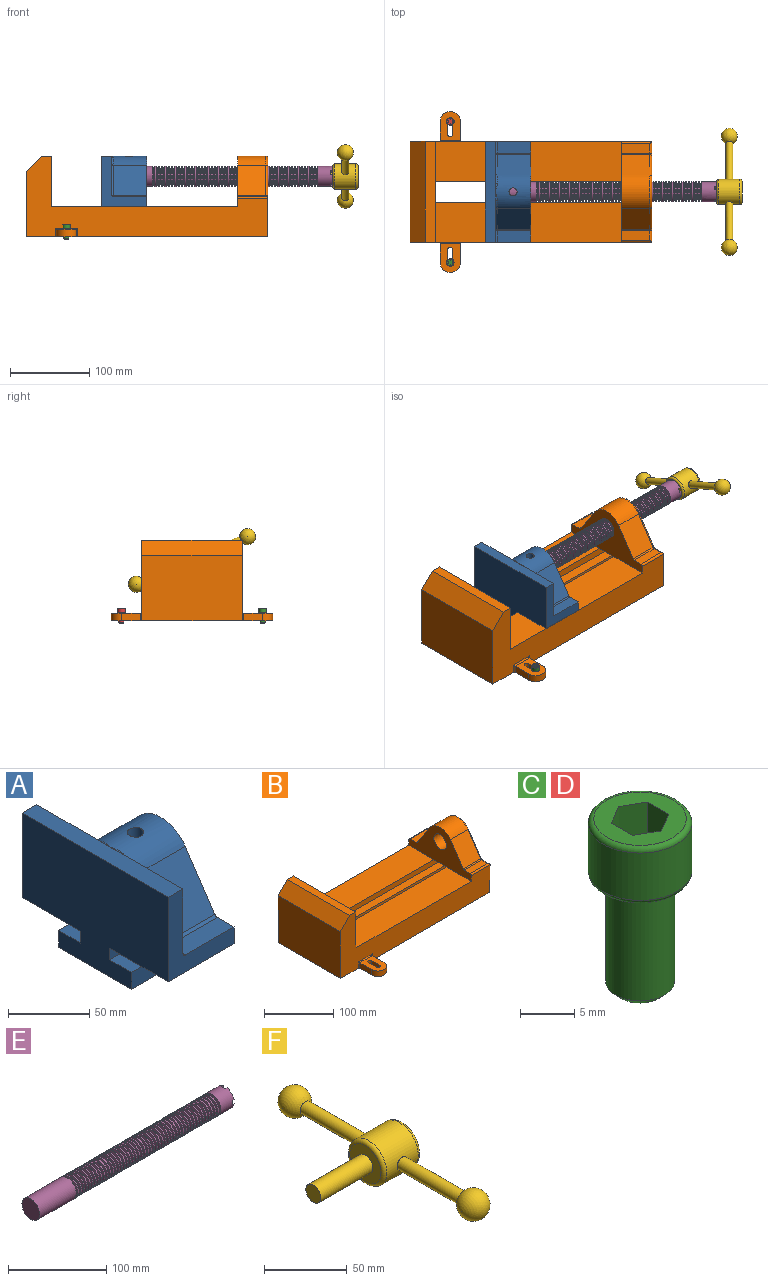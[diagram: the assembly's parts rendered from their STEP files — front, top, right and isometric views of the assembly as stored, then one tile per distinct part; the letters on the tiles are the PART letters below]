
ASSEMBLY  parts=6 mates=6
PART A: 36 faces, bbox 57.2x127x89 mm
  f0: plane 57.15x50.8mm, normal (0,0,-1), area 2903.2mm2, adj f6,f9,f10,f23
  f1: cylinder r=12.7mm len=44.45mm, axis (1,0,0), area 3464.3mm2, adj f6,f15,f16
  f2: plane 41.91x14.52mm, normal (0,0,1), area 608.5mm2, adj f6,f11,f24,f25
  f3: plane 51.86x48.26mm, normal (1,0,0), area 1495.7mm2, adj f8,f10,f31,f33,f35
  f4: plane 51.86x48.26mm, normal (1,0,0), area 1495.7mm2, adj f8,f11,f24,f28,f29
  f5: plane 57.15x50.8mm, normal (0,0,-1), area 2903.2mm2, adj f6,f9,f11,f22
  f6: plane 127x85.09mm, normal (1,0,0), area 5190.6mm2, adj f0,f1,f2,f5,f7,f10,f11,f12
  f7: plane 41.91x14.52mm, normal (0,0,1), area 608.5mm2, adj f6,f10,f30,f31
  f8: plane 127x12.7mm, normal (0,0,1), area 1612.9mm2, adj f3,f4,f9,f10,f11,f26,f34
  f9: plane 127x85.09mm, normal (-1,0,0), area 9096.8mm2, adj f0,f5,f8,f10,f11,f17,f18,f19
  f10: plane 63.5x57.15mm, normal (0,-1,0), area 1372.3mm2, adj f0,f3,f6,f7,f8,f9,f31
  f11: plane 63.5x57.15mm, normal (0,1,0), area 1372.3mm2, adj f2,f4,f5,f6,f8,f9,f24
  f12: plane 41.91x38.43mm, normal (0,-0.83,0.56), area 1939.2mm2, adj f6,f13,f30,f33
  f13: cylinder r=25.4mm len=44.45mm, axis (1,0,0), area 2026.5mm2, adj f6,f12,f14,f16,f26,f28,f34,f35
  f14: plane 41.91x38.43mm, normal (0,0.83,0.56), area 1939.2mm2, adj f6,f13,f25,f29
  f15: plane 25.4x25.4mm, normal (1,0,0), area 506.7mm2, adj f1
  f16: cylinder r=5.08mm len=13.76mm, axis (0,0,1), area 414mm2, adj f1,f13
  f17: plane 57.15x19.05mm, normal (0,0,1), area 1088.7mm2, adj f6,f9,f18,f23
  f18: plane 57.15x12.7mm, normal (0,-1,0), area 725.8mm2, adj f6,f9,f17,f19
  f19: plane 63.5x57.15mm, normal (0,0,-1), area 3629mm2, adj f6,f9,f18,f20
  f20: plane 57.15x12.7mm, normal (0,1,0), area 725.8mm2, adj f6,f9,f19,f21
  f21: plane 57.15x19.05mm, normal (0,0,1), area 1088.7mm2, adj f6,f9,f20,f22
  f22: plane 57.15x8.89mm, normal (0,1,0), area 508.1mm2, adj f5,f6,f9,f21
  f23: plane 57.15x8.89mm, normal (0,-1,0), area 508.1mm2, adj f0,f6,f9,f17
  f24: cylinder r=2.54mm len=14.52mm, axis (0,-1,0), area 57.9mm2, adj f2,f4,f11,f27
  f25: cylinder r=2.54mm len=41.91mm, axis (1,0,0), area 104.3mm2, adj f2,f6,f14,f27
  f26: bspline ~12.24x2.8mm, area 20.9mm2, adj f8,f13,f28
  f27: sphere r=2.54mm, area 6.3mm2, adj f24,f25,f29
  f28: torus R=27.94mm, axis (1,0,0), area 57.8mm2, adj f4,f13,f26,f29
  f29: cylinder r=2.54mm len=39.84mm, axis (0,-0.56,0.83), area 184.6mm2, adj f4,f14,f27,f28
  f30: cylinder r=2.54mm len=41.91mm, axis (1,0,0), area 104.3mm2, adj f6,f7,f12,f32
  f31: cylinder r=2.54mm len=14.52mm, axis (0,-1,0), area 57.9mm2, adj f3,f7,f10,f32
  f32: sphere r=2.54mm, area 6.3mm2, adj f30,f31,f33
  f33: cylinder r=2.54mm len=39.84mm, axis (0,-0.56,-0.83), area 184.6mm2, adj f3,f12,f32,f35
  f34: bspline ~12.24x2.8mm, area 20.9mm2, adj f8,f13,f35
  f35: torus R=27.94mm, axis (1,0,0), area 57.8mm2, adj f3,f13,f33,f34
PART B: 61 faces, bbox 304.8x203.2x103.7 mm
  f0: plane 304.8x101.6mm, normal (0,1,0), area 13520.3mm2, adj f3,f4,f5,f6,f7,f8,f9,f16
  f1: plane 304.8x101.6mm, normal (0,-1,0), area 13520.3mm2, adj f2,f3,f5,f6,f7,f8,f9,f16
  f2: plane 234.95x50.8mm, normal (0,0,1), area 11935.5mm2, adj f1,f5,f16,f26
  f3: plane 127x99.06mm, normal (1,0,0), area 7097.5mm2, adj f0,f1,f9,f14,f17,f18,f19,f20
  f4: plane 234.95x50.8mm, normal (0,0,1), area 11935.5mm2, adj f0,f5,f16,f27
  f5: plane 127x101.6mm, normal (1,0,0), area 9516.1mm2, adj f0,f1,f2,f4,f6,f9,f18,f19
  f6: plane 127x12.7mm, normal (0,0,1), area 1612.9mm2, adj f0,f1,f5,f7
  f7: plane 127x19.05mm, normal (-0.71,0,0.71), area 3421.5mm2, adj f0,f1,f6,f8
  f8: plane 127x82.55mm, normal (-1,0,0), area 10483.8mm2, adj f0,f1,f7,f9
  f9: plane 304.8x203.2mm, normal (0,0,-1), area 33298.3mm2, adj f0,f1,f3,f5,f8,f21,f22,f39
  f10: plane 35.56x11.98mm, normal (0,0,1), area 426mm2, adj f16,f28,f29,f30
  f11: plane 38.43x35.56mm, normal (0,0.83,0.56), area 1645.4mm2, adj f12,f16,f29,f32
  f12: cylinder r=25.4mm len=42.19mm, axis (1,0,0), area 1770.2mm2, adj f11,f13,f16,f33
  f13: plane 38.43x35.56mm, normal (0,-0.83,0.56), area 1645.4mm2, adj f12,f16,f34,f35
  f14: cylinder r=12.7mm len=38.1mm, axis (1,0,0), area 3040.2mm2, adj f3,f16
  f15: plane 35.56x11.98mm, normal (0,0,1), area 426mm2, adj f16,f34,f36,f38
  f16: plane 127x63.5mm, normal (-1,0,0), area 4155.5mm2, adj f0,f1,f2,f4,f10,f11,f12,f13
  f17: plane 38.1x25.4mm, normal (0,0,-1), area 967.7mm2, adj f3,f16,f26,f27
  f18: plane 273.05x19.05mm, normal (0,0,-1), area 5201.6mm2, adj f3,f5,f19,f26
  f19: plane 273.05x12.7mm, normal (0,1,0), area 3467.7mm2, adj f3,f5,f18,f20
  f20: plane 273.05x19.05mm, normal (0,0,1), area 5201.6mm2, adj f3,f5,f19,f21
  f21: plane 273.05x16.51mm, normal (0,1,0), area 4508.1mm2, adj f3,f5,f9,f20
  f22: plane 273.05x16.51mm, normal (0,-1,0), area 4508.1mm2, adj f3,f5,f9,f23
  f23: plane 273.05x19.05mm, normal (0,0,1), area 5201.6mm2, adj f3,f5,f22,f24
  f24: plane 273.05x12.7mm, normal (0,-1,0), area 3467.7mm2, adj f3,f5,f23,f25
  f25: plane 273.05x19.05mm, normal (0,0,-1), area 5201.6mm2, adj f3,f5,f24,f27
  f26: plane 273.05x8.89mm, normal (0,1,0), area 2427.4mm2, adj f2,f3,f5,f17,f18
  f27: plane 273.05x8.89mm, normal (0,-1,0), area 2427.4mm2, adj f3,f4,f5,f17,f25
  f28: cylinder r=2.54mm len=38.1mm, axis (1,0,0), area 148.3mm2, adj f0,f10,f16,f30
  f29: cylinder r=2.54mm len=35.56mm, axis (-1,0,0), area 88.5mm2, adj f10,f11,f16,f31
  f30: cylinder r=2.54mm len=14.52mm, axis (0,1,0), area 54.3mm2, adj f3,f10,f28,f31
  f31: torus R=5.08mm, axis (-1,0,0), area 13.5mm2, adj f3,f29,f30,f32
  f32: cylinder r=2.54mm len=39.84mm, axis (0,0.56,-0.83), area 184.6mm2, adj f3,f11,f31,f33
  f33: torus R=22.86mm, axis (-1,0,0), area 191.4mm2, adj f3,f12,f32,f35
  f34: cylinder r=2.54mm len=35.56mm, axis (-1,0,0), area 88.5mm2, adj f13,f15,f16,f37
  f35: cylinder r=2.54mm len=39.84mm, axis (0,0.56,0.83), area 184.6mm2, adj f3,f13,f33,f37
  f36: cylinder r=2.54mm len=38.1mm, axis (-1,0,0), area 148.3mm2, adj f1,f15,f16,f38
  f37: torus R=5.08mm, axis (-1,0,0), area 13.5mm2, adj f3,f34,f35,f38
  f38: cylinder r=2.54mm len=14.52mm, axis (0,1,0), area 54.3mm2, adj f3,f15,f36,f37
  f39: plane 23.88x9.53mm, normal (-1,0,0), area 227.4mm2, adj f9,f45,f46,f60
  f40: plane 23.88x9.53mm, normal (1,0,0), area 227.4mm2, adj f9,f45,f46,f58
  f41: cylinder r=3.3mm len=9.53mm, axis (0,0,-1), area 98.8mm2, adj f9,f42,f44,f46
  f42: plane 15.62x9.53mm, normal (-1,0,0), area 148.8mm2, adj f9,f41,f43,f46
  f43: cylinder r=3.3mm len=9.53mm, axis (0,0,-1), area 98.8mm2, adj f9,f42,f44,f46
  f44: plane 15.62x9.53mm, normal (1,0,0), area 148.8mm2, adj f9,f41,f43,f46
  f45: cylinder r=12.7mm len=25.4mm, axis (0,0,-1), area 380mm2, adj f9,f39,f40,f46
  f46: plane 36.58x25.4mm, normal (0,0,1), area 722.4mm2, adj f39,f40,f41,f42,f43,f44,f45,f59
  f47: plane 23.88x9.53mm, normal (-1,0,0), area 227.4mm2, adj f9,f53,f54,f56
  f48: plane 23.88x9.53mm, normal (1,0,0), area 227.4mm2, adj f9,f53,f54,f55
  f49: cylinder r=3.3mm len=9.53mm, axis (0,0,-1), area 98.8mm2, adj f9,f50,f52,f54
  f50: plane 15.62x9.53mm, normal (-1,0,0), area 148.8mm2, adj f9,f49,f51,f54
  f51: cylinder r=3.3mm len=9.53mm, axis (0,0,-1), area 98.8mm2, adj f9,f50,f52,f54
  f52: plane 15.62x9.53mm, normal (1,0,0), area 148.8mm2, adj f9,f49,f51,f54
  f53: cylinder r=12.7mm len=25.4mm, axis (0,0,-1), area 380mm2, adj f9,f47,f48,f54
  f54: plane 36.58x25.4mm, normal (0,0,1), area 722.4mm2, adj f47,f48,f49,f50,f51,f52,f53,f57
  f55: cylinder r=1.52mm len=11.05mm, axis (0,0,-1), area 24.1mm2, adj f0,f9,f48,f57
  f56: cylinder r=1.52mm len=11.05mm, axis (0,0,1), area 24.1mm2, adj f0,f9,f47,f57
  f57: cylinder r=1.52mm len=28.45mm, axis (1,0,0), area 63.5mm2, adj f0,f54,f55,f56
  f58: cylinder r=1.52mm len=11.05mm, axis (0,0,1), area 24.1mm2, adj f1,f9,f40,f59
  f59: cylinder r=1.52mm len=28.45mm, axis (-1,0,0), area 63.5mm2, adj f1,f46,f58,f60
  f60: cylinder r=1.52mm len=11.05mm, axis (0,0,-1), area 24.1mm2, adj f1,f9,f39,f59
PART C: 15 faces, bbox 10.3x10.3x19.1 mm
  f0: plane 8.51x8.51mm, normal (0,0,1), area 37.2mm2, adj f5,f6,f7,f8,f9,f10,f14
  f1: cylinder r=3.17mm len=11.94mm, axis (0,0,1), area 238.2mm2, adj f4,f12
  f2: plane 4.83x4.83mm, normal (0,0,-1), area 18.3mm2, adj f12
  f3: cylinder r=4.76mm len=9.53mm, axis (0,0,-1), area 159.6mm2, adj f13,f14
  f4: plane 8.51x8.51mm, normal (0,0,-1), area 25.2mm2, adj f1,f13
  f5: plane 4.83x2.38mm, normal (-0.5,-0.87,0), area 13.3mm2, adj f0,f6,f10,f11
  f6: plane 4.83x2.38mm, normal (0.5,-0.87,0), area 13.3mm2, adj f0,f5,f7,f11
  f7: plane 4.83x2.75mm, normal (1,0,0), area 13.3mm2, adj f0,f6,f8,f11
  f8: plane 4.83x2.38mm, normal (0.5,0.87,0), area 13.3mm2, adj f0,f7,f9,f11
  f9: plane 4.83x2.38mm, normal (-0.5,0.87,0), area 13.3mm2, adj f0,f8,f10,f11
  f10: plane 4.83x2.75mm, normal (-1,0,0), area 13.3mm2, adj f0,f5,f9,f11
  f11: plane 5.5x4.76mm, normal (0,0,1), area 19.6mm2, adj f5,f6,f7,f8,f9,f10
  f12: cone r=3.17mm half-angle=45deg, axis (0,0,1), area 18.9mm2, adj f1,f2
  f13: torus R=4.25mm, axis (0,0,1), area 23mm2, adj f3,f4
  f14: torus R=4.25mm, axis (0,0,1), area 23mm2, adj f0,f3
PART D: same geometry as C
PART E: 220 faces, bbox 279.4x25.4x25.4 mm
  f0: cylinder r=12.7mm len=25.4mm, axis (-1,0,0), area 1468.2mm2, adj f1,f2,f3,f5,f7,f208,f209,f210
  f1: plane 9.9x9.9mm, normal (1,0,0), area 62.3mm2, adj f0,f4,f213,f216
  f2: plane 9.9x9.9mm, normal (1,0,0), area 62.3mm2, adj f0,f4,f210,f218
  f3: plane 9.9x9.9mm, normal (1,0,0), area 62.3mm2, adj f0,f4,f209,f212
  f4: cylinder r=6.35mm len=25.4mm, axis (1,0,0), area 960.3mm2, adj f1,f2,f3,f5,f6,f208,f209,f210
  f5: plane 9.9x9.9mm, normal (1,0,0), area 62.3mm2, adj f0,f4,f215,f217
  f6: plane 12.7x12.7mm, normal (1,0,0), area 126.7mm2, adj f4
  f7: cone r=12.7mm half-angle=76deg, axis (1,0,0), area 188mm2, adj f0,f9
  f8: cone r=10.16mm half-angle=76deg, axis (-1,0,0), area 188mm2, adj f9,f10
  f9: cylinder r=10.16mm len=20.32mm, axis (1,0,0), area 81.1mm2, adj f7,f8
  f10: cylinder r=12.7mm len=25.4mm, axis (-1,0,0), area 131.7mm2, adj f8,f11
  f11: cone r=12.7mm half-angle=76deg, axis (1,0,0), area 188mm2, adj f10,f13
  f12: cone r=10.16mm half-angle=76deg, axis (-1,0,0), area 188mm2, adj f13,f14
  f13: cylinder r=10.16mm len=20.32mm, axis (1,0,0), area 81.1mm2, adj f11,f12
  f14: cylinder r=12.7mm len=25.4mm, axis (-1,0,0), area 131.7mm2, adj f12,f15
  f15: cone r=12.7mm half-angle=76deg, axis (1,0,0), area 188mm2, adj f14,f17
  f16: cone r=10.16mm half-angle=76deg, axis (-1,0,0), area 188mm2, adj f17,f18
  f17: cylinder r=10.16mm len=20.32mm, axis (1,0,0), area 81.1mm2, adj f15,f16
  f18: cylinder r=12.7mm len=25.4mm, axis (-1,0,0), area 131.7mm2, adj f16,f19
  f19: cone r=12.7mm half-angle=76deg, axis (1,0,0), area 188mm2, adj f18,f21
  f20: cone r=10.16mm half-angle=76deg, axis (-1,0,0), area 188mm2, adj f21,f22
  f21: cylinder r=10.16mm len=20.32mm, axis (1,0,0), area 81.1mm2, adj f19,f20
  f22: cylinder r=12.7mm len=25.4mm, axis (-1,0,0), area 131.7mm2, adj f20,f23
  f23: cone r=12.7mm half-angle=76deg, axis (1,0,0), area 188mm2, adj f22,f25
  f24: cone r=10.16mm half-angle=76deg, axis (-1,0,0), area 188mm2, adj f25,f26
  f25: cylinder r=10.16mm len=20.32mm, axis (1,0,0), area 81.1mm2, adj f23,f24
  f26: cylinder r=12.7mm len=25.4mm, axis (-1,0,0), area 131.7mm2, adj f24,f27
  f27: cone r=12.7mm half-angle=76deg, axis (1,0,0), area 188mm2, adj f26,f29
  f28: cone r=10.16mm half-angle=76deg, axis (-1,0,0), area 188mm2, adj f29,f30
  f29: cylinder r=10.16mm len=20.32mm, axis (1,0,0), area 81.1mm2, adj f27,f28
  f30: cylinder r=12.7mm len=25.4mm, axis (-1,0,0), area 131.7mm2, adj f28,f31
  f31: cone r=12.7mm half-angle=76deg, axis (1,0,0), area 188mm2, adj f30,f33
  f32: cone r=10.16mm half-angle=76deg, axis (-1,0,0), area 188mm2, adj f33,f34
  f33: cylinder r=10.16mm len=20.32mm, axis (1,0,0), area 81.1mm2, adj f31,f32
  f34: cylinder r=12.7mm len=25.4mm, axis (-1,0,0), area 131.7mm2, adj f32,f35
  f35: cone r=12.7mm half-angle=76deg, axis (1,0,0), area 188mm2, adj f34,f37
  f36: cone r=10.16mm half-angle=76deg, axis (-1,0,0), area 188mm2, adj f37,f38
  f37: cylinder r=10.16mm len=20.32mm, axis (1,0,0), area 81.1mm2, adj f35,f36
  f38: cylinder r=12.7mm len=25.4mm, axis (-1,0,0), area 131.7mm2, adj f36,f39
  f39: cone r=12.7mm half-angle=76deg, axis (1,0,0), area 188mm2, adj f38,f41
  f40: cone r=10.16mm half-angle=76deg, axis (-1,0,0), area 188mm2, adj f41,f42
  f41: cylinder r=10.16mm len=20.32mm, axis (1,0,0), area 81.1mm2, adj f39,f40
  f42: cylinder r=12.7mm len=25.4mm, axis (-1,0,0), area 131.7mm2, adj f40,f43
  f43: cone r=12.7mm half-angle=76deg, axis (1,0,0), area 188mm2, adj f42,f45
  f44: cone r=10.16mm half-angle=76deg, axis (-1,0,0), area 188mm2, adj f45,f46
  f45: cylinder r=10.16mm len=20.32mm, axis (1,0,0), area 81.1mm2, adj f43,f44
  f46: cylinder r=12.7mm len=25.4mm, axis (-1,0,0), area 131.7mm2, adj f44,f47
  f47: cone r=12.7mm half-angle=76deg, axis (1,0,0), area 188mm2, adj f46,f49
  f48: cone r=10.16mm half-angle=76deg, axis (-1,0,0), area 188mm2, adj f49,f50
  f49: cylinder r=10.16mm len=20.32mm, axis (1,0,0), area 81.1mm2, adj f47,f48
  f50: cylinder r=12.7mm len=25.4mm, axis (-1,0,0), area 131.7mm2, adj f48,f51
  f51: cone r=12.7mm half-angle=76deg, axis (1,0,0), area 188mm2, adj f50,f53
  f52: cone r=10.16mm half-angle=76deg, axis (-1,0,0), area 188mm2, adj f53,f54
  f53: cylinder r=10.16mm len=20.32mm, axis (1,0,0), area 81.1mm2, adj f51,f52
  f54: cylinder r=12.7mm len=25.4mm, axis (-1,0,0), area 131.7mm2, adj f52,f55
  f55: cone r=12.7mm half-angle=76deg, axis (1,0,0), area 188mm2, adj f54,f57
  f56: cone r=10.16mm half-angle=76deg, axis (-1,0,0), area 188mm2, adj f57,f58
  f57: cylinder r=10.16mm len=20.32mm, axis (1,0,0), area 81.1mm2, adj f55,f56
  f58: cylinder r=12.7mm len=25.4mm, axis (-1,0,0), area 131.7mm2, adj f56,f59
  f59: cone r=12.7mm half-angle=76deg, axis (1,0,0), area 188mm2, adj f58,f61
  f60: cone r=10.16mm half-angle=76deg, axis (-1,0,0), area 188mm2, adj f61,f62
  f61: cylinder r=10.16mm len=20.32mm, axis (1,0,0), area 81.1mm2, adj f59,f60
  f62: cylinder r=12.7mm len=25.4mm, axis (-1,0,0), area 131.7mm2, adj f60,f63
  f63: cone r=12.7mm half-angle=76deg, axis (1,0,0), area 188mm2, adj f62,f65
  f64: cone r=10.16mm half-angle=76deg, axis (-1,0,0), area 188mm2, adj f65,f66
  f65: cylinder r=10.16mm len=20.32mm, axis (1,0,0), area 81.1mm2, adj f63,f64
  f66: cylinder r=12.7mm len=25.4mm, axis (-1,0,0), area 131.7mm2, adj f64,f67
  f67: cone r=12.7mm half-angle=76deg, axis (1,0,0), area 188mm2, adj f66,f69
  f68: cone r=10.16mm half-angle=76deg, axis (-1,0,0), area 188mm2, adj f69,f70
  f69: cylinder r=10.16mm len=20.32mm, axis (1,0,0), area 81.1mm2, adj f67,f68
  f70: cylinder r=12.7mm len=25.4mm, axis (-1,0,0), area 131.7mm2, adj f68,f71
  f71: cone r=12.7mm half-angle=76deg, axis (1,0,0), area 188mm2, adj f70,f73
  f72: cone r=10.16mm half-angle=76deg, axis (-1,0,0), area 188mm2, adj f73,f74
  f73: cylinder r=10.16mm len=20.32mm, axis (1,0,0), area 81.1mm2, adj f71,f72
  f74: cylinder r=12.7mm len=25.4mm, axis (-1,0,0), area 131.7mm2, adj f72,f75
  f75: cone r=12.7mm half-angle=76deg, axis (1,0,0), area 188mm2, adj f74,f77
  f76: cone r=10.16mm half-angle=76deg, axis (-1,0,0), area 188mm2, adj f77,f78
  f77: cylinder r=10.16mm len=20.32mm, axis (1,0,0), area 81.1mm2, adj f75,f76
  f78: cylinder r=12.7mm len=25.4mm, axis (-1,0,0), area 131.7mm2, adj f76,f79
  f79: cone r=12.7mm half-angle=76deg, axis (1,0,0), area 188mm2, adj f78,f81
  f80: cone r=10.16mm half-angle=76deg, axis (-1,0,0), area 188mm2, adj f81,f82
  f81: cylinder r=10.16mm len=20.32mm, axis (1,0,0), area 81.1mm2, adj f79,f80
  f82: cylinder r=12.7mm len=25.4mm, axis (-1,0,0), area 131.7mm2, adj f80,f83
  f83: cone r=12.7mm half-angle=76deg, axis (1,0,0), area 188mm2, adj f82,f85
  f84: cone r=10.16mm half-angle=76deg, axis (-1,0,0), area 188mm2, adj f85,f86
  f85: cylinder r=10.16mm len=20.32mm, axis (1,0,0), area 81.1mm2, adj f83,f84
  f86: cylinder r=12.7mm len=25.4mm, axis (-1,0,0), area 131.7mm2, adj f84,f87
  f87: cone r=12.7mm half-angle=76deg, axis (1,0,0), area 188mm2, adj f86,f89
  f88: cone r=10.16mm half-angle=76deg, axis (-1,0,0), area 188mm2, adj f89,f90
  f89: cylinder r=10.16mm len=20.32mm, axis (1,0,0), area 81.1mm2, adj f87,f88
  f90: cylinder r=12.7mm len=25.4mm, axis (-1,0,0), area 131.7mm2, adj f88,f91
  f91: cone r=12.7mm half-angle=76deg, axis (1,0,0), area 188mm2, adj f90,f93
  f92: cone r=10.16mm half-angle=76deg, axis (-1,0,0), area 188mm2, adj f93,f94
  f93: cylinder r=10.16mm len=20.32mm, axis (1,0,0), area 81.1mm2, adj f91,f92
  f94: cylinder r=12.7mm len=25.4mm, axis (-1,0,0), area 131.7mm2, adj f92,f95
  f95: cone r=12.7mm half-angle=76deg, axis (1,0,0), area 188mm2, adj f94,f97
  f96: cone r=10.16mm half-angle=76deg, axis (-1,0,0), area 188mm2, adj f97,f98
  f97: cylinder r=10.16mm len=20.32mm, axis (1,0,0), area 81.1mm2, adj f95,f96
  f98: cylinder r=12.7mm len=25.4mm, axis (-1,0,0), area 131.7mm2, adj f96,f99
  f99: cone r=12.7mm half-angle=76deg, axis (1,0,0), area 188mm2, adj f98,f101
  f100: cone r=10.16mm half-angle=76deg, axis (-1,0,0), area 188mm2, adj f101,f102
  f101: cylinder r=10.16mm len=20.32mm, axis (1,0,0), area 81.1mm2, adj f99,f100
  f102: cylinder r=12.7mm len=25.4mm, axis (-1,0,0), area 131.7mm2, adj f100,f103
  f103: cone r=12.7mm half-angle=76deg, axis (1,0,0), area 188mm2, adj f102,f105
  f104: cone r=10.16mm half-angle=76deg, axis (-1,0,0), area 188mm2, adj f105,f106
  f105: cylinder r=10.16mm len=20.32mm, axis (1,0,0), area 81.1mm2, adj f103,f104
  f106: cylinder r=12.7mm len=25.4mm, axis (-1,0,0), area 131.7mm2, adj f104,f107
  f107: cone r=12.7mm half-angle=76deg, axis (1,0,0), area 188mm2, adj f106,f109
  f108: cone r=10.16mm half-angle=76deg, axis (-1,0,0), area 188mm2, adj f109,f110
  f109: cylinder r=10.16mm len=20.32mm, axis (1,0,0), area 81.1mm2, adj f107,f108
  f110: cylinder r=12.7mm len=25.4mm, axis (-1,0,0), area 131.7mm2, adj f108,f111
  f111: cone r=12.7mm half-angle=76deg, axis (1,0,0), area 188mm2, adj f110,f113
  f112: cone r=10.16mm half-angle=76deg, axis (-1,0,0), area 188mm2, adj f113,f114
  f113: cylinder r=10.16mm len=20.32mm, axis (1,0,0), area 81.1mm2, adj f111,f112
  f114: cylinder r=12.7mm len=25.4mm, axis (-1,0,0), area 131.7mm2, adj f112,f115
  f115: cone r=12.7mm half-angle=76deg, axis (1,0,0), area 188mm2, adj f114,f117
  f116: cone r=10.16mm half-angle=76deg, axis (-1,0,0), area 188mm2, adj f117,f118
  f117: cylinder r=10.16mm len=20.32mm, axis (1,0,0), area 81.1mm2, adj f115,f116
  f118: cylinder r=12.7mm len=25.4mm, axis (-1,0,0), area 131.7mm2, adj f116,f119
  f119: cone r=12.7mm half-angle=76deg, axis (1,0,0), area 188mm2, adj f118,f121
  f120: cone r=10.16mm half-angle=76deg, axis (-1,0,0), area 188mm2, adj f121,f122
  f121: cylinder r=10.16mm len=20.32mm, axis (1,0,0), area 81.1mm2, adj f119,f120
  f122: cylinder r=12.7mm len=25.4mm, axis (-1,0,0), area 131.7mm2, adj f120,f123
  f123: cone r=12.7mm half-angle=76deg, axis (1,0,0), area 188mm2, adj f122,f125
  f124: cone r=10.16mm half-angle=76deg, axis (-1,0,0), area 188mm2, adj f125,f126
  f125: cylinder r=10.16mm len=20.32mm, axis (1,0,0), area 81.1mm2, adj f123,f124
  f126: cylinder r=12.7mm len=25.4mm, axis (-1,0,0), area 131.7mm2, adj f124,f127
  f127: cone r=12.7mm half-angle=76deg, axis (1,0,0), area 188mm2, adj f126,f129
  f128: cone r=10.16mm half-angle=76deg, axis (-1,0,0), area 188mm2, adj f129,f130
  f129: cylinder r=10.16mm len=20.32mm, axis (1,0,0), area 81.1mm2, adj f127,f128
  f130: cylinder r=12.7mm len=25.4mm, axis (-1,0,0), area 131.7mm2, adj f128,f131
  f131: cone r=12.7mm half-angle=76deg, axis (1,0,0), area 188mm2, adj f130,f133
  f132: cone r=10.16mm half-angle=76deg, axis (-1,0,0), area 188mm2, adj f133,f134
  f133: cylinder r=10.16mm len=20.32mm, axis (1,0,0), area 81.1mm2, adj f131,f132
  f134: cylinder r=12.7mm len=25.4mm, axis (-1,0,0), area 131.7mm2, adj f132,f135
  f135: cone r=12.7mm half-angle=76deg, axis (1,0,0), area 188mm2, adj f134,f137
  f136: cone r=10.16mm half-angle=76deg, axis (-1,0,0), area 188mm2, adj f137,f138
  f137: cylinder r=10.16mm len=20.32mm, axis (1,0,0), area 81.1mm2, adj f135,f136
  f138: cylinder r=12.7mm len=25.4mm, axis (-1,0,0), area 131.7mm2, adj f136,f139
  f139: cone r=12.7mm half-angle=76deg, axis (1,0,0), area 188mm2, adj f138,f141
  f140: cone r=10.16mm half-angle=76deg, axis (-1,0,0), area 188mm2, adj f141,f142
  f141: cylinder r=10.16mm len=20.32mm, axis (1,0,0), area 81.1mm2, adj f139,f140
  f142: cylinder r=12.7mm len=25.4mm, axis (-1,0,0), area 131.7mm2, adj f140,f143
  f143: cone r=12.7mm half-angle=76deg, axis (1,0,0), area 188mm2, adj f142,f145
  f144: cone r=10.16mm half-angle=76deg, axis (-1,0,0), area 188mm2, adj f145,f146
  f145: cylinder r=10.16mm len=20.32mm, axis (1,0,0), area 81.1mm2, adj f143,f144
  f146: cylinder r=12.7mm len=25.4mm, axis (-1,0,0), area 131.7mm2, adj f144,f147
  f147: cone r=12.7mm half-angle=76deg, axis (1,0,0), area 188mm2, adj f146,f149
  f148: cone r=10.16mm half-angle=76deg, axis (-1,0,0), area 188mm2, adj f149,f150
  f149: cylinder r=10.16mm len=20.32mm, axis (1,0,0), area 81.1mm2, adj f147,f148
  f150: cylinder r=12.7mm len=25.4mm, axis (-1,0,0), area 131.7mm2, adj f148,f151
  f151: cone r=12.7mm half-angle=76deg, axis (1,0,0), area 188mm2, adj f150,f153
  f152: cone r=10.16mm half-angle=76deg, axis (-1,0,0), area 188mm2, adj f153,f154
  f153: cylinder r=10.16mm len=20.32mm, axis (1,0,0), area 81.1mm2, adj f151,f152
  f154: cylinder r=12.7mm len=25.4mm, axis (-1,0,0), area 131.7mm2, adj f152,f155
  f155: cone r=12.7mm half-angle=76deg, axis (1,0,0), area 188mm2, adj f154,f157
  f156: cone r=10.16mm half-angle=76deg, axis (-1,0,0), area 188mm2, adj f157,f158
  f157: cylinder r=10.16mm len=20.32mm, axis (1,0,0), area 81.1mm2, adj f155,f156
  f158: cylinder r=12.7mm len=25.4mm, axis (-1,0,0), area 131.7mm2, adj f156,f159
  f159: cone r=12.7mm half-angle=76deg, axis (1,0,0), area 188mm2, adj f158,f161
  f160: cone r=10.16mm half-angle=76deg, axis (-1,0,0), area 188mm2, adj f161,f162
  f161: cylinder r=10.16mm len=20.32mm, axis (1,0,0), area 81.1mm2, adj f159,f160
  f162: cylinder r=12.7mm len=25.4mm, axis (-1,0,0), area 131.7mm2, adj f160,f163
  f163: cone r=12.7mm half-angle=76deg, axis (1,0,0), area 188mm2, adj f162,f165
  f164: cone r=10.16mm half-angle=76deg, axis (-1,0,0), area 188mm2, adj f165,f166
  f165: cylinder r=10.16mm len=20.32mm, axis (1,0,0), area 81.1mm2, adj f163,f164
  f166: cylinder r=12.7mm len=25.4mm, axis (-1,0,0), area 131.7mm2, adj f164,f167
  f167: cone r=12.7mm half-angle=76deg, axis (1,0,0), area 188mm2, adj f166,f169
  f168: cone r=10.16mm half-angle=76deg, axis (-1,0,0), area 188mm2, adj f169,f170
  f169: cylinder r=10.16mm len=20.32mm, axis (1,0,0), area 81.1mm2, adj f167,f168
  f170: cylinder r=12.7mm len=25.4mm, axis (-1,0,0), area 131.7mm2, adj f168,f171
  f171: cone r=12.7mm half-angle=76deg, axis (1,0,0), area 188mm2, adj f170,f173
  f172: cone r=10.16mm half-angle=76deg, axis (-1,0,0), area 188mm2, adj f173,f174
  f173: cylinder r=10.16mm len=20.32mm, axis (1,0,0), area 81.1mm2, adj f171,f172
  f174: cylinder r=12.7mm len=25.4mm, axis (-1,0,0), area 131.7mm2, adj f172,f175
  f175: cone r=12.7mm half-angle=76deg, axis (1,0,0), area 188mm2, adj f174,f177
  f176: cone r=10.16mm half-angle=76deg, axis (-1,0,0), area 188mm2, adj f177,f178
  f177: cylinder r=10.16mm len=20.32mm, axis (1,0,0), area 81.1mm2, adj f175,f176
  f178: cylinder r=12.7mm len=25.4mm, axis (-1,0,0), area 131.7mm2, adj f176,f179
  f179: cone r=12.7mm half-angle=76deg, axis (1,0,0), area 188mm2, adj f178,f181
  f180: cone r=10.16mm half-angle=76deg, axis (-1,0,0), area 188mm2, adj f181,f182
  f181: cylinder r=10.16mm len=20.32mm, axis (1,0,0), area 81.1mm2, adj f179,f180
  f182: cylinder r=12.7mm len=25.4mm, axis (-1,0,0), area 131.7mm2, adj f180,f183
  f183: cone r=12.7mm half-angle=76deg, axis (1,0,0), area 188mm2, adj f182,f185
  f184: cone r=10.16mm half-angle=76deg, axis (-1,0,0), area 188mm2, adj f185,f186
  f185: cylinder r=10.16mm len=20.32mm, axis (1,0,0), area 81.1mm2, adj f183,f184
  f186: cylinder r=12.7mm len=25.4mm, axis (-1,0,0), area 131.7mm2, adj f184,f187
  f187: cone r=12.7mm half-angle=76deg, axis (1,0,0), area 188mm2, adj f186,f189
  f188: cone r=10.16mm half-angle=76deg, axis (-1,0,0), area 188mm2, adj f189,f190
  f189: cylinder r=10.16mm len=20.32mm, axis (1,0,0), area 81.1mm2, adj f187,f188
  f190: cylinder r=12.7mm len=25.4mm, axis (-1,0,0), area 131.7mm2, adj f188,f191
  f191: cone r=12.7mm half-angle=76deg, axis (1,0,0), area 188mm2, adj f190,f193
  f192: cone r=10.16mm half-angle=76deg, axis (-1,0,0), area 188mm2, adj f193,f194
  f193: cylinder r=10.16mm len=20.32mm, axis (1,0,0), area 81.1mm2, adj f191,f192
  f194: cylinder r=12.7mm len=25.4mm, axis (-1,0,0), area 131.7mm2, adj f192,f195
  f195: cone r=12.7mm half-angle=76deg, axis (1,0,0), area 188mm2, adj f194,f197
  f196: cone r=10.16mm half-angle=76deg, axis (-1,0,0), area 188mm2, adj f197,f198
  f197: cylinder r=10.16mm len=20.32mm, axis (1,0,0), area 81.1mm2, adj f195,f196
  f198: cylinder r=12.7mm len=25.4mm, axis (-1,0,0), area 131.7mm2, adj f196,f199
  f199: cone r=12.7mm half-angle=76deg, axis (1,0,0), area 188mm2, adj f198,f201
  f200: cone r=10.16mm half-angle=76deg, axis (-1,0,0), area 188mm2, adj f201,f202
  f201: cylinder r=10.16mm len=20.32mm, axis (1,0,0), area 81.1mm2, adj f199,f200
  f202: cylinder r=12.7mm len=25.4mm, axis (-1,0,0), area 131.7mm2, adj f200,f203
  f203: cone r=12.7mm half-angle=76deg, axis (1,0,0), area 188mm2, adj f202,f205
  f204: cone r=10.16mm half-angle=76deg, axis (-1,0,0), area 188mm2, adj f205,f207
  f205: cylinder r=10.16mm len=20.32mm, axis (1,0,0), area 81.1mm2, adj f203,f204
  f206: plane 25.4x25.4mm, normal (-1,0,0), area 506.7mm2, adj f207
  f207: cylinder r=12.7mm len=52.45mm, axis (-1,0,0), area 4185.4mm2, adj f204,f206
  f208: plane 6.88x5.08mm, normal (1,0,0), area 32.7mm2, adj f0,f4,f209,f210
  f209: plane 6.62x2.54mm, normal (0,-1,0), area 16.8mm2, adj f0,f3,f4,f208
  f210: plane 6.62x2.54mm, normal (0,1,0), area 16.8mm2, adj f0,f2,f4,f208
  f211: plane 6.88x5.08mm, normal (1,0,0), area 32.7mm2, adj f0,f4,f212,f213
  f212: plane 6.62x2.54mm, normal (0,0,1), area 16.8mm2, adj f0,f3,f4,f211
  f213: plane 6.62x2.54mm, normal (0,0,-1), area 16.8mm2, adj f0,f1,f4,f211
  f214: plane 6.88x5.08mm, normal (1,0,0), area 32.7mm2, adj f0,f4,f215,f216
  f215: plane 6.62x2.54mm, normal (0,1,0), area 16.8mm2, adj f0,f4,f5,f214
  f216: plane 6.62x2.54mm, normal (0,-1,0), area 16.8mm2, adj f0,f1,f4,f214
  f217: plane 6.62x2.54mm, normal (0,0,-1), area 16.8mm2, adj f0,f4,f5,f219
  f218: plane 6.62x2.54mm, normal (0,0,1), area 16.8mm2, adj f0,f2,f4,f219
  f219: plane 6.88x5.08mm, normal (1,0,0), area 32.7mm2, adj f0,f4,f217,f218
PART F: 11 faces, bbox 76.2x172.7x34.4 mm
  f0: sphere r=10.16mm, area 1231.8mm2, adj f1
  f1: cylinder r=4.45mm len=51.82mm, axis (0,1,0), area 1438.5mm2, adj f0,f4
  f2: sphere r=10.16mm, area 1231.8mm2, adj f3
  f3: cylinder r=4.45mm len=51.82mm, axis (0,1,0), area 1438.5mm2, adj f2,f4
  f4: cylinder r=15.88mm len=31.75mm, axis (-1,0,0), area 2534.7mm2, adj f1,f3,f9,f10
  f5: cylinder r=6.35mm len=44.45mm, axis (-1,0,0), area 1773.5mm2, adj f6,f8
  f6: plane 12.7x12.7mm, normal (-1,0,0), area 126.7mm2, adj f5
  f7: plane 26.67x26.67mm, normal (1,0,0), area 558.6mm2, adj f10
  f8: plane 26.67x26.67mm, normal (-1,0,0), area 432mm2, adj f5,f9
  f9: torus R=13.33mm, axis (1,0,0), area 374.8mm2, adj f4,f8
  f10: torus R=13.33mm, axis (1,0,0), area 374.8mm2, adj f4,f7
PLACE A t=(63.19,12.07,-5)mm
PLACE B t=(0,12.07,-5)mm fixed
PLACE C t=(-254,-76.83,4.53)mm
PLACE D rot(axis=(0,0,1),180deg) t=(-254,100.97,4.53)mm
PLACE E rot(axis=(1,0,0),156.8deg) t=(62.92,42.04,141.26)mm
PLACE F rot(axis=(1,0,0),156.8deg) t=(43.87,42.04,141.26)mm
MATE pin_slot C.f1 <-> B.f41  axis (0,0,1) through (-254,-76.83,4.53)mm
MATE fastened F.f5 <-> E.f4  axis (-1,0,0) through (81.97,12.07,71.2)mm
MATE revolute E.f7 <-> A.f28  axis (-1,0,0) through (-197.43,12.07,71.2)mm
MATE pin_slot D.f1 <-> B.f49  axis (0,0,1) through (-254,100.97,4.53)mm
MATE slider A.f6 <-> B.f5  axis (1,0,0) through (-152.71,-19.68,24.21)mm
MATE cylindrical E.f7 <-> B.f12  axis (1,0,0) through (-119.83,12.07,71.2)mm
